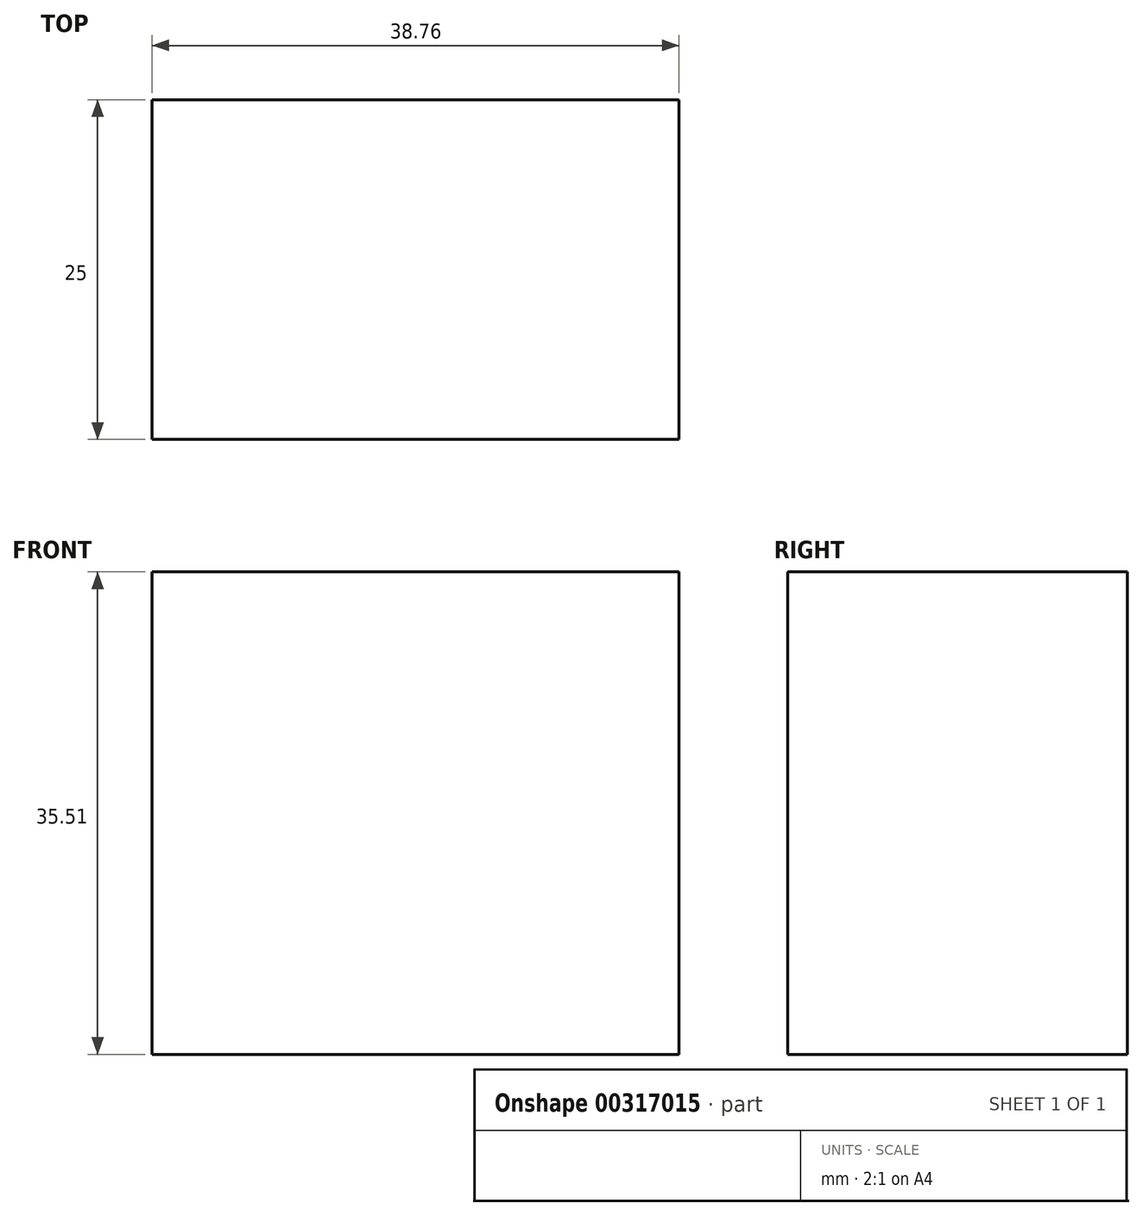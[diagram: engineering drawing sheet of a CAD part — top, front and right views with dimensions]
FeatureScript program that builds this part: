
annotation { "Feature Type Name" : "Feature", "Feature Type Description" : "" }
export const myFeature = defineFeature(function(context is Context, id is Id, definition is map)
    precondition{}
    {
        {
            var Q0;
            Q0=qCreatedBy(makeId("Front.planeOp"),FACE);
            var sketch = newSketch(context, id + "F0", { "sketchPlane" : qUnion([Q0])});
            skLineSegment(sketch, "E0.bottom", {"start": v(0, 0) * mm, "end": v(38.76, 0) * mm});
            skLineSegment(sketch, "E0.top", {"start": v(0, 35.51) * mm, "end": v(38.76, 35.51) * mm});
            skLineSegment(sketch, "E0.left", {"start": v(0, 0) * mm, "end": v(0, 35.51) * mm});
            skLineSegment(sketch, "E0.right", {"start": v(38.76, 0) * mm, "end": v(38.76, 35.51) * mm});
            skSolve(sketch);
        }
        {
            var Q0;
            Q0=makeQuery(id+"F0.imprint","IMPRINT",FACE,{"disambiguationData":[TD([[makeQuery(id+"F0.imprint","IMPRINT",EDGE,{"derivedFrom":sQuery(id+"F0.wireOp",EDGE,"E0.bottom")}),1.0]])]});
            extrude(context, id + "F1", {"entities" : qUnion([Q0]), "depth" : 25 * mm});
        }
    });
